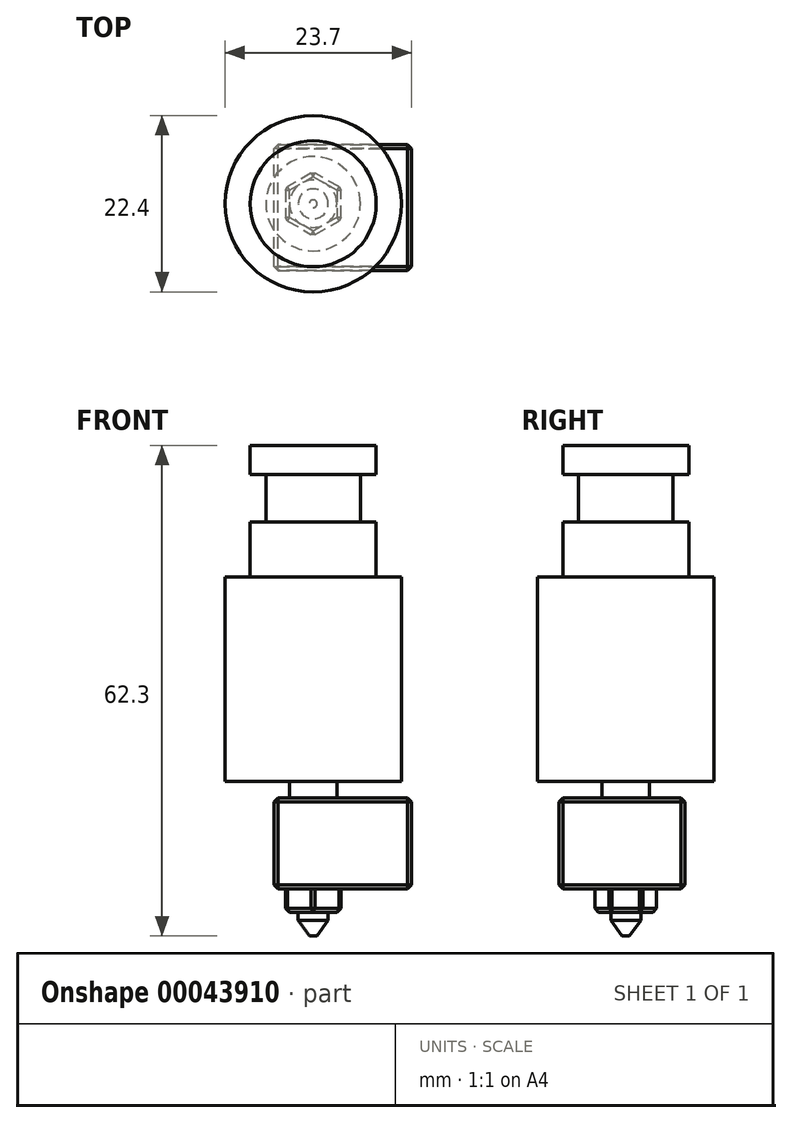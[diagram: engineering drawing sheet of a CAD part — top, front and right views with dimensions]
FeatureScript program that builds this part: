
annotation { "Feature Type Name" : "Feature", "Feature Type Description" : "" }
export const myFeature = defineFeature(function(context is Context, id is Id, definition is map)
    precondition{}
    {
        {
            var Q0;
            Q0=qCreatedBy(makeId("Front.planeOp"),FACE);
            var sketch = newSketch(context, id + "F0", { "sketchPlane" : qUnion([Q0])});
            skLineSegment(sketch, "E0", {"start": v(0, 0) * mm, "end": v(0, 41.77) * mm, "construction": true});
            skLineSegment(sketch, "E1", {"start": v(0, 30) * mm, "end": v(-8, 30) * mm});
            skLineSegment(sketch, "E2", {"start": v(-8, 30) * mm, "end": v(-8, 26.3) * mm});
            skLineSegment(sketch, "E3", {"start": v(-8, 26.3) * mm, "end": v(-6, 26.3) * mm});
            skLineSegment(sketch, "E4", {"start": v(-6, 26.3) * mm, "end": v(-6, 20.3) * mm});
            skLineSegment(sketch, "E5", {"start": v(-6, 20.3) * mm, "end": v(-8, 20.3) * mm});
            skLineSegment(sketch, "E6", {"start": v(-8, 20.3) * mm, "end": v(-8, 13.3) * mm});
            skLineSegment(sketch, "E7", {"start": v(-8, 13.3) * mm, "end": v(-11.2, 13.3) * mm});
            skLineSegment(sketch, "E8", {"start": v(-11.2, 13.3) * mm, "end": v(-11.2, -12.7) * mm});
            skLineSegment(sketch, "E9", {"start": v(-11.2, -12.7) * mm, "end": v(-3, -12.7) * mm});
            skLineSegment(sketch, "E10", {"start": v(-3, -12.7) * mm, "end": v(-3, -28.73) * mm});
            skLineSegment(sketch, "E11", {"start": v(-1.9, -30.3) * mm, "end": v(-0.5, -32.3) * mm});
            skLineSegment(sketch, "E12", {"start": v(-0.5, -32.3) * mm, "end": v(0, -32.3) * mm});
            skLineSegment(sketch, "E13", {"start": v(0, -32.3) * mm, "end": v(0, 30) * mm});
            skLineSegment(sketch, "E14", {"start": v(-3, -28.73) * mm, "end": v(-1.9, -28.73) * mm});
            skLineSegment(sketch, "E15", {"start": v(-1.9, -28.73) * mm, "end": v(-1.9, -30.3) * mm});
            skSolve(sketch);
        }
        {
            var Q0;
            Q0=makeQuery(id+"F0.imprint","IMPRINT",FACE,{"disambiguationData":[TD([[makeQuery(id+"F0.imprint","IMPRINT",EDGE,{"derivedFrom":sQuery(id+"F0.wireOp",EDGE,"E1")}),1.0]])]});
            var Q1;
            Q1=sQuery(id+"F0.wireOp",EDGE,"E0");
            revolve(context, id + "F1", {"entities" : qUnion([Q0]), "axis" : qUnion([Q1]), "revolveType" : RevolveType.FULL});
        }
        {
            var Q0;
            Q0=makeQuery(id+"F1.opRevolve","SWEPT_FACE",FACE,{"disambiguationData":[OSD([sQuery(id+"F0.wireOp",EDGE,"E9")])]});
            var sketch = newSketch(context, id + "F2", { "sketchPlane" : qUnion([Q0])});
            skLineSegment(sketch, "E16.bottom", {"start": v(-5, 8.5) * mm, "end": v(12.5, 8.5) * mm});
            skLineSegment(sketch, "E16.top", {"start": v(-5, -7.5) * mm, "end": v(12.5, -7.5) * mm});
            skLineSegment(sketch, "E16.left", {"start": v(-5, 8.5) * mm, "end": v(-5, -7.5) * mm});
            skLineSegment(sketch, "E16.right", {"start": v(12.5, 8.5) * mm, "end": v(12.5, -7.5) * mm});
            skSolve(sketch);
        }
        {
            var Q0;
            {var subQ6=sQuery(id+"F2.wireOp",EDGE,"E16.left");Q0=makeQuery(id+"F2.imprint","IMPRINT",FACE,{"disambiguationData":[TD([[makeQuery(id+"F2.imprint","IMPRINT",EDGE,{"derivedFrom":subQ6}),1.0]])]});}
            var Q1;
            {var subQ5=sQuery(id+"F2.wireOp",EDGE,"E16.right");Q1=makeQuery(id+"F2.imprint","IMPRINT",FACE,{"disambiguationData":[TD([[makeQuery(id+"F2.imprint","IMPRINT",EDGE,{"derivedFrom":subQ5}),-1.0]])]});}
            extrude(context, id + "F3", {"entities" : qUnion([Q0, Q1]), "operationType" : NewBodyOperationType.ADD, "depth" : 13.6 * mm, "hasSecondDirection" : true, "secondDirectionOppositeDirection" : false, "secondDirectionDepth" : 2.1 * mm});
        }
        {
            var Q0;
            Q0=makeQuery(id+"F3.opExtrude","CAP_FACE",FACE,{"disambiguationData":[OSD([sQuery(id+"F0.wireOp",EDGE,"E9"),sQuery(id+"F0.wireOp",EDGE,"E10"),sQuery(id+"F2.wireOp",EDGE,"E16.bottom"),sQuery(id+"F2.wireOp",EDGE,"E16.top"),sQuery(id+"F2.wireOp",EDGE,"E16.left"),sQuery(id+"F2.wireOp",EDGE,"E16.right")])],"isStart":false});
            var sketch = newSketch(context, id + "F4", { "sketchPlane" : qUnion([Q0])});
            skCircle(sketch, "E17.cCircle", {"center": v(0, 0) * mm, "radius": 3.5 * mm, "construction": true});
            skLineSegment(sketch, "E17.0", {"start": v(3.5, 2.02) * mm, "end": v(3.5, -2.02) * mm});
            skLineSegment(sketch, "E17.1", {"start": v(3.5, -2.02) * mm, "end": v(0, -4.04) * mm});
            skLineSegment(sketch, "E17.2", {"start": v(0, -4.04) * mm, "end": v(-3.5, -2.02) * mm});
            skLineSegment(sketch, "E17.3", {"start": v(-3.5, -2.02) * mm, "end": v(-3.5, 2.02) * mm});
            skLineSegment(sketch, "E17.4", {"start": v(-3.5, 2.02) * mm, "end": v(0, 4.04) * mm});
            skLineSegment(sketch, "E17.5", {"start": v(0, 4.04) * mm, "end": v(3.5, 2.02) * mm});
            skPoint(sketch, "E17.0.midPoint", {"position": v(3.5, 0) * mm});
            skSolve(sketch);
        }
        {
            var Q0;
            Q0=qSketchRegion(id+"F4",true);
            extrude(context, id + "F5", {"entities" : qUnion([Q0]), "operationType" : NewBodyOperationType.ADD, "depth" : 3 * mm});
        }
        {
            var Q0;
            Q0=makeQuery(id+"F3.opExtrude","SWEPT_FACE",FACE,{"disambiguationData":[OSD([sQuery(id+"F2.wireOp",EDGE,"E16.bottom")])]});
            var Q1;
            Q1=makeQuery(id+"F3.opExtrude","SWEPT_FACE",FACE,{"disambiguationData":[OSD([sQuery(id+"F2.wireOp",EDGE,"E16.left")])]});
            var Q2;
            Q2=makeQuery(id+"F3.opExtrude","SWEPT_FACE",FACE,{"disambiguationData":[OSD([sQuery(id+"F2.wireOp",EDGE,"E16.right")])]});
            var Q3;
            Q3=makeQuery(id+"F3.opExtrude","SWEPT_FACE",FACE,{"disambiguationData":[OSD([sQuery(id+"F2.wireOp",EDGE,"E16.top")])]});
            var Q4;
            Q4=makeQuery(id+"F5.opExtrude","CAP_EDGE",EDGE,{"disambiguationData":[OSD([sQuery(id+"F4.wireOp",EDGE,"E17.1")])],"isStart":false});
            var Q5;
            Q5=makeQuery(id+"F5.opExtrude","CAP_EDGE",EDGE,{"disambiguationData":[OSD([sQuery(id+"F4.wireOp",EDGE,"E17.2")])],"isStart":false});
            var Q6;
            Q6=makeQuery(id+"F5.opExtrude","CAP_EDGE",EDGE,{"disambiguationData":[OSD([sQuery(id+"F4.wireOp",EDGE,"E17.0")])],"isStart":false});
            var Q7;
            Q7=makeQuery(id+"F5.opExtrude","SWEPT_EDGE",EDGE,{"disambiguationData":[OSD([sQuery(id+"F4.wireOp",EDGE,"E17.1"),sQuery(id+"F4.wireOp",EDGE,"E17.2")])]});
            var Q8;
            Q8=makeQuery(id+"F5.opExtrude","SWEPT_EDGE",EDGE,{"disambiguationData":[OSD([sQuery(id+"F4.wireOp",EDGE,"E17.2"),sQuery(id+"F4.wireOp",EDGE,"E17.3")])]});
            var Q9;
            Q9=makeQuery(id+"F5.opExtrude","CAP_EDGE",EDGE,{"disambiguationData":[OSD([sQuery(id+"F4.wireOp",EDGE,"E17.3")])],"isStart":false});
            var Q10;
            Q10=makeQuery(id+"F5.opExtrude","SWEPT_EDGE",EDGE,{"disambiguationData":[OSD([sQuery(id+"F4.wireOp",EDGE,"E17.3"),sQuery(id+"F4.wireOp",EDGE,"E17.4")])]});
            var Q11;
            Q11=makeQuery(id+"F5.opExtrude","CAP_EDGE",EDGE,{"disambiguationData":[OSD([sQuery(id+"F4.wireOp",EDGE,"E17.4")])],"isStart":false});
            var Q12;
            Q12=makeQuery(id+"F5.opExtrude","SWEPT_EDGE",EDGE,{"disambiguationData":[OSD([sQuery(id+"F4.wireOp",EDGE,"E17.4"),sQuery(id+"F4.wireOp",EDGE,"E17.5")])]});
            var Q13;
            Q13=makeQuery(id+"F5.opExtrude","CAP_EDGE",EDGE,{"disambiguationData":[OSD([sQuery(id+"F4.wireOp",EDGE,"E17.5")])],"isStart":false});
            var Q14;
            Q14=makeQuery(id+"F5.opExtrude","SWEPT_EDGE",EDGE,{"disambiguationData":[OSD([sQuery(id+"F4.wireOp",EDGE,"E17.0"),sQuery(id+"F4.wireOp",EDGE,"E17.5")])]});
            var Q15;
            Q15=makeQuery(id+"F5.opExtrude","SWEPT_EDGE",EDGE,{"disambiguationData":[OSD([sQuery(id+"F4.wireOp",EDGE,"E17.0"),sQuery(id+"F4.wireOp",EDGE,"E17.1")])]});
            chamfer(context, id + "F6", {"entities" : qUnion([Q0, Q1, Q2, Q3, Q4, Q5, Q6, Q7, Q8, Q9, Q10, Q11, Q12, Q13, Q14, Q15]), "width" : 0.5 * mm, "tangentPropagation" : true});
        }
    });
